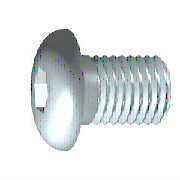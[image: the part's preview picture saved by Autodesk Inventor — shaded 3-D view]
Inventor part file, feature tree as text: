
AUTODESK INVENTOR PART (.ipt)
format: ipt  version: 2013 (Build 170138000, 138)  size: 191,488 bytes
history: native  units: mm (DEFAULTED — no unit token found)
features: sketch x2, extrude x1, plane x1
ambient origin geometry x7: Origin, YZ Plane, XY Plane, X Axis, Y Axis, Z Axis, Center Point
bodies: Solid1 (feature_tree), Body (feature_tree)
feature tree (4):
  extrude  "Slot"  Depth=0.49076mm
  plane  "Work Plane1"
  sketch  "Sketch1"  dims[d0=18.4mm d1=0.49076mm]
  sketch  "Sketch2"  dims[d2=2.75mm d3=1.56mm d4=60.0deg d5=5.0mm d6=5.0mm d7=3.464102mm d8=9.5mm d10=90.0deg d11=10.0mm d9=0.0mm d12=18.4mm d13=0.0mm d14=0.49076mm d15=0.49076mm d16=2.375mm d17=0.0mm d18=0.0mm d19=20.0mm d27=45.0deg d28=0.2mm d29=0.2mm]
